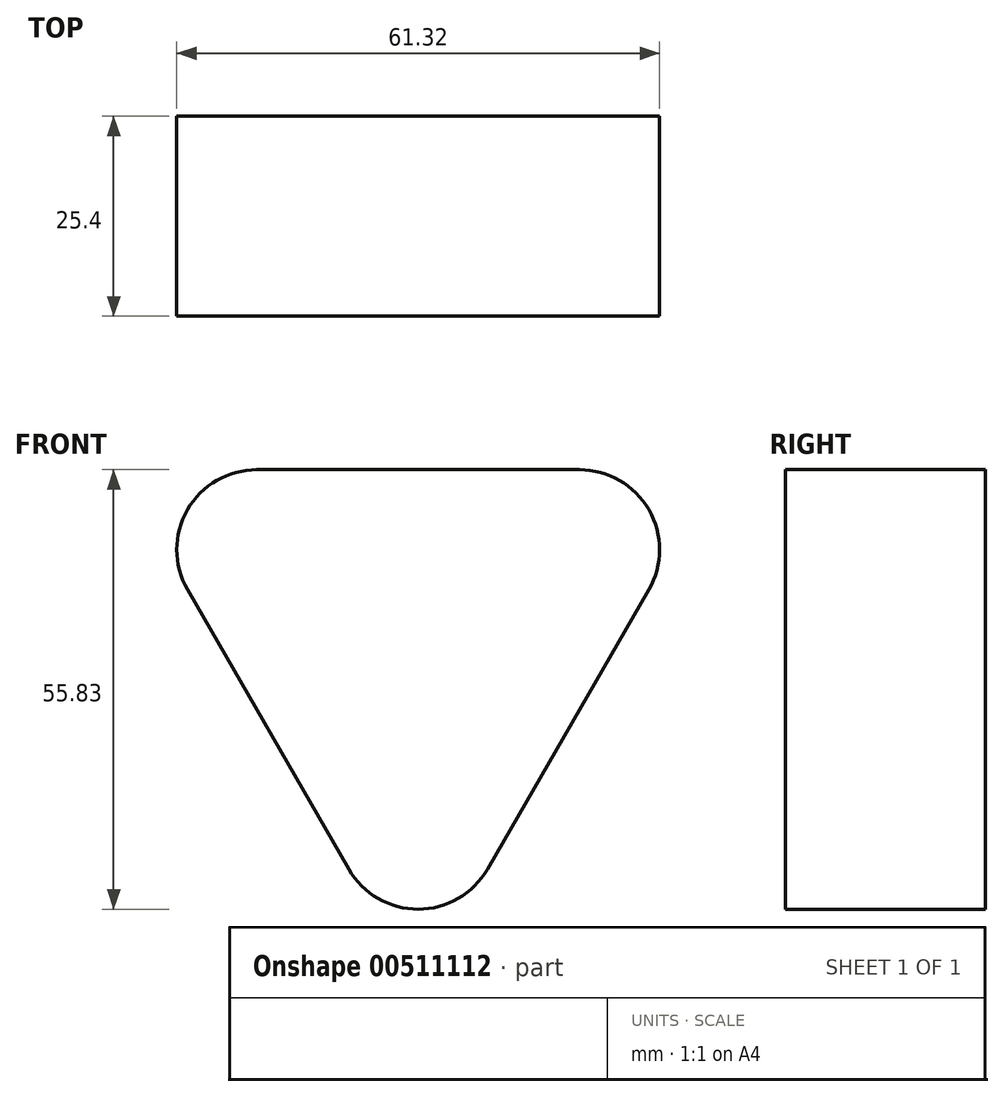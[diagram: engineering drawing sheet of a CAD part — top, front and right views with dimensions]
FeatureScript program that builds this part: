
annotation { "Feature Type Name" : "Feature", "Feature Type Description" : "" }
export const myFeature = defineFeature(function(context is Context, id is Id, definition is map)
    precondition{}
    {
        {
            var Q0;
            Q0=qCreatedBy(makeId("Front.planeOp"),FACE);
            var sketch = newSketch(context, id + "F0", { "sketchPlane" : qUnion([Q0])});
            skLineSegment(sketch, "E0", {"start": v(-8.8, -20.43) * mm, "end": v(-29.3, 15.08) * mm});
            skLineSegment(sketch, "E1", {"start": v(-20.5, 30.32) * mm, "end": v(20.5, 30.32) * mm});
            skLineSegment(sketch, "E2", {"start": v(29.3, 15.08) * mm, "end": v(8.8, -20.43) * mm});
            skPoint(sketch, "E3.visualSharp", {"position": v(0, -35.67) * mm});
            skArc(sketch, "E3.filletArc", {"start": v(-8.8, -20.43) * mm, "mid": v(0, -25.51) * mm, "end": v(8.8, -20.43) * mm});
            skPoint(sketch, "E4.visualSharp", {"position": v(-38.1, 30.32) * mm});
            skArc(sketch, "E4.filletArc", {"start": v(-20.5, 30.32) * mm, "mid": v(-29.3, 25.24) * mm, "end": v(-29.3, 15.08) * mm});
            skPoint(sketch, "E5.visualSharp", {"position": v(38.1, 30.32) * mm});
            skArc(sketch, "E5.filletArc", {"start": v(29.3, 15.08) * mm, "mid": v(29.3, 25.24) * mm, "end": v(20.5, 30.32) * mm});
            skSolve(sketch);
        }
        {
            var Q0;
            Q0=makeQuery(id+"F0.imprint","IMPRINT",FACE,{"disambiguationData":[TD([[makeQuery(id+"F0.imprint","IMPRINT",EDGE,{"derivedFrom":sQuery(id+"F0.wireOp",EDGE,"E0")}),-1.0]])]});
            extrude(context, id + "F1", {"entities" : qUnion([Q0]), "depth" : 25.4 * mm});
        }
    });
